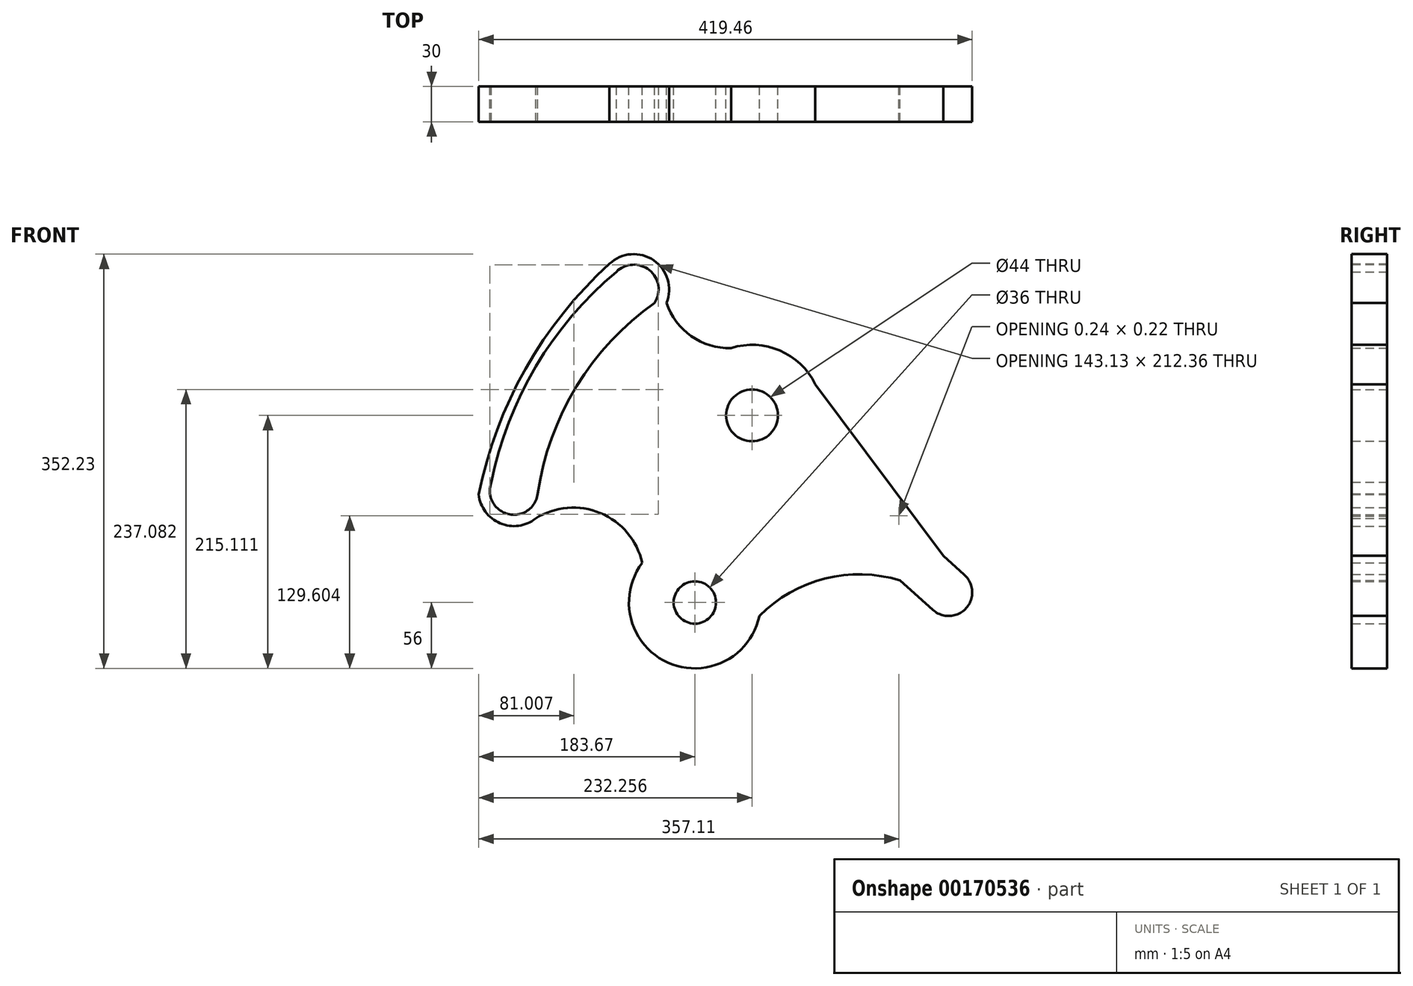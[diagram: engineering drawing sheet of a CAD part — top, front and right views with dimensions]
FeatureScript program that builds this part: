
annotation { "Feature Type Name" : "Feature", "Feature Type Description" : "" }
export const myFeature = defineFeature(function(context is Context, id is Id, definition is map)
    precondition{}
    {
        {
            var Q0;
            Q0=qCreatedBy(makeId("Front.planeOp"),FACE);
            var sketch = newSketch(context, id + "F0", { "sketchPlane" : qUnion([Q0])});
            skCircle(sketch, "E0", {"center": v(0, 0) * mm, "radius": 56 * mm});
            skCircle(sketch, "E1", {"center": v(0, 0) * mm, "radius": 18 * mm});
            skArc(sketch, "E2", {"start": v(-183.67, 91.86) * mm, "mid": v(-165.52, 67.38) * mm, "end": v(-135.32, 71.42) * mm});
            skArc(sketch, "E3", {"start": v(102.39, 185.67) * mm, "mid": v(72.23, 214.25) * mm, "end": v(30.74, 216.4) * mm});
            skCircle(sketch, "E4", {"center": v(48.59, 159.11) * mm, "radius": 42 * mm});
            skCircle(sketch, "E5", {"center": v(48.59, 159.11) * mm, "radius": 22 * mm});
            skLineSegment(sketch, "E6", {"start": v(48.59, 159.11) * mm, "end": v(-302.12, 159.11) * mm, "construction": true});
            skLineSegment(sketch, "E7", {"start": v(48.59, 159.11) * mm, "end": v(-229.5, 409.5) * mm, "construction": true});
            skLineSegment(sketch, "E8", {"start": v(48.59, 159.11) * mm, "end": v(442.92, -195.95) * mm, "construction": true});
            skArc(sketch, "E9", {"start": v(173.56, 73.5) * mm, "mid": v(145.25, 72.19) * mm, "end": v(146.67, 43.88) * mm});
            skArc(sketch, "E10", {"start": v(202.41, -6.3) * mm, "mid": v(230.71, -4.76) * mm, "end": v(229.05, 23.53) * mm});
            skLineSegment(sketch, "E11", {"start": v(146.67, 43.88) * mm, "end": v(202.41, -6.3) * mm});
            skLineSegment(sketch, "E12", {"start": v(173.32, 73.71) * mm, "end": v(229.05, 23.53) * mm});
            skArc(sketch, "E13", {"start": v(174.54, 18.79) * mm, "mid": v(110.53, 20.31) * mm, "end": v(54.85, -11.3) * mm});
            skArc(sketch, "E14", {"start": v(-44.72, 33.7) * mm, "mid": v(-80.23, 76.07) * mm, "end": v(-135.32, 71.42) * mm});
            skLineSegment(sketch, "E15", {"start": v(211.15, 39.65) * mm, "end": v(102.39, 185.67) * mm});
            skArc(sketch, "E16", {"start": v(-24.12, 254.87) * mm, "mid": v(-3.08, 226.52) * mm, "end": v(30.74, 216.4) * mm});
            skArc(sketch, "E17", {"start": v(-24.12, 254.87) * mm, "mid": v(-34.92, 290.97) * mm, "end": v(-72.48, 288.04) * mm});
            skArc(sketch, "E18", {"start": v(-72.48, 288.04) * mm, "mid": v(-143.84, 198.88) * mm, "end": v(-183.67, 91.86) * mm});
            skArc(sketch, "E19", {"start": v(-172.86, 102.42) * mm, "mid": v(-158.91, 75.24) * mm, "end": v(-133.6, 92.34) * mm});
            skArc(sketch, "E20", {"start": v(-66.72, 281.18) * mm, "mid": v(-135.06, 200.86) * mm, "end": v(-172.86, 102.42) * mm});
            skArc(sketch, "E21", {"start": v(-34.15, 254.87) * mm, "mid": v(-100.68, 183.6) * mm, "end": v(-133.67, 91.86) * mm});
            skArc(sketch, "E22.trimOffspring", {"start": v(-34.15, 254.87) * mm, "mid": v(-38.65, 282.61) * mm, "end": v(-66.72, 281.18) * mm});
            skPoint(sketch, "E23.orphan", {"position": v(-174.25, 95.02) * mm});
            skSolve(sketch);
        }
        {
            var Q0;
            Q0=makeQuery(id+"F0.imprint","IMPRINT",FACE,{"disambiguationData":[TD([[makeQuery(id+"F0.imprint","IMPRINT",EDGE,{"derivedFrom":sQuery(id+"F0.wireOp",EDGE,"E1")}),-1.0]])]});
            var Q1;
            Q1=makeQuery(id+"F0.imprint","IMPRINT",FACE,{"disambiguationData":[TD([[makeQuery(id+"F0.imprint","IMPRINT",EDGE,{"derivedFrom":sQuery(id+"F0.wireOp",EDGE,"E4")}),1.0]])]});
            var Q2;
            Q2=makeQuery(id+"F0.imprint","IMPRINT",FACE,{"disambiguationData":[TD([[makeQuery(id+"F0.imprint","IMPRINT",EDGE,{"derivedFrom":sQuery(id+"F0.wireOp",EDGE,"E2")}),1.0]])]});
            var Q3;
            {var subQ1=sQuery(id+"F0.wireOp",EDGE,"E10");Q3=makeQuery(id+"F0.imprint","IMPRINT",FACE,{"disambiguationData":[TD([[makeQuery(id+"F0.imprint","IMPRINT",EDGE,{"derivedFrom":subQ1}),1.0]])]});}
            extrude(context, id + "F1", {"entities" : qUnion([Q0, Q1, Q2, Q3]), "depth" : 30 * mm});
        }
    });
